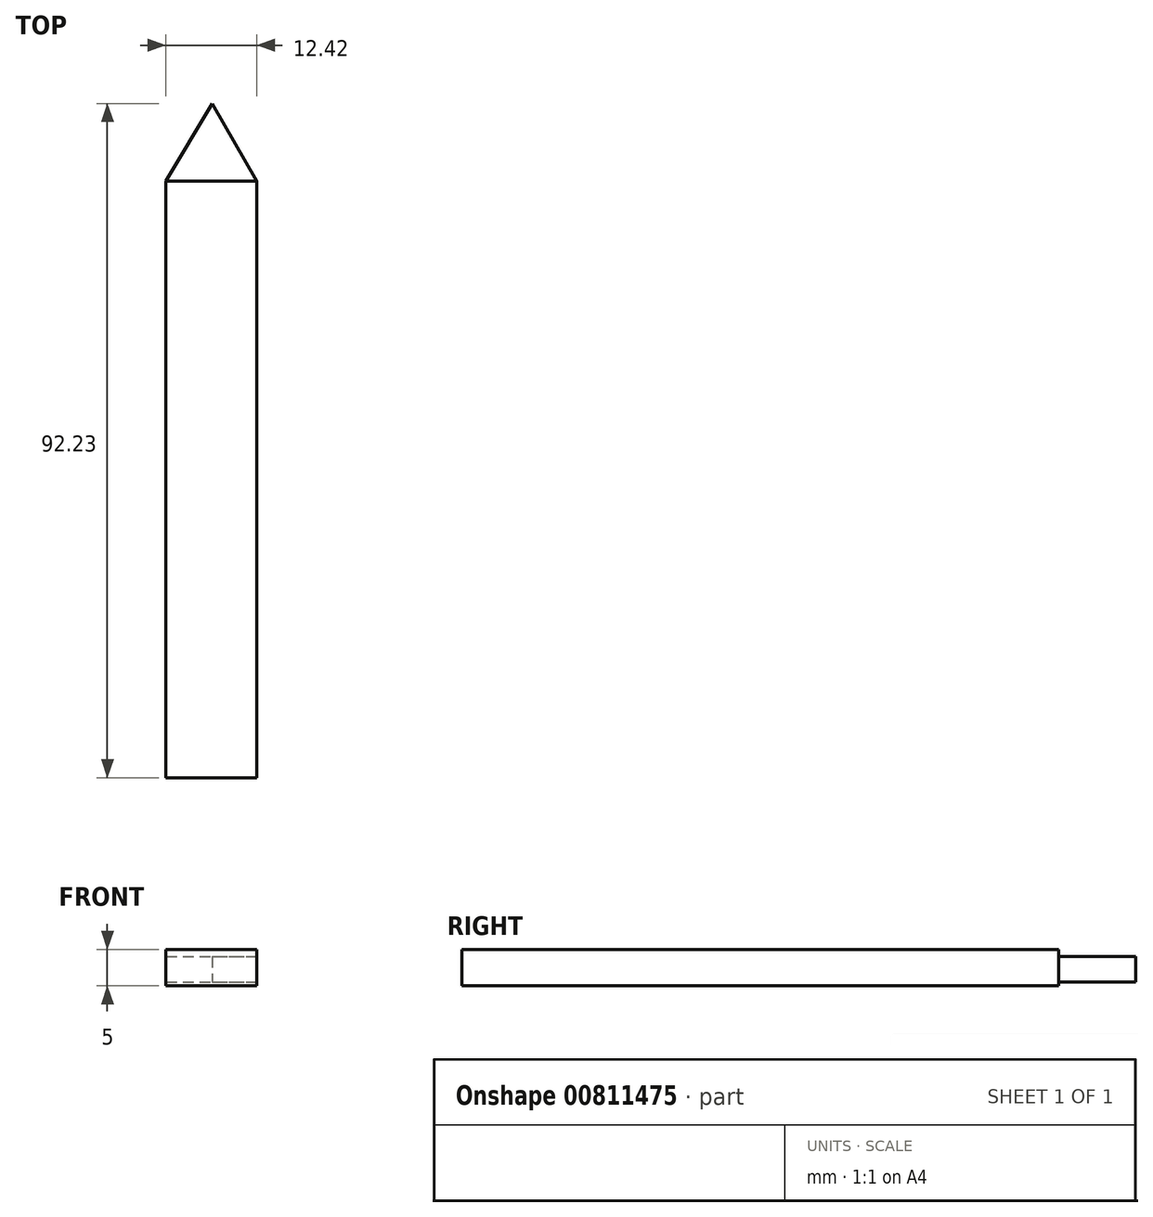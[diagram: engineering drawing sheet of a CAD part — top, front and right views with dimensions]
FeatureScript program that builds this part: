
annotation { "Feature Type Name" : "Feature", "Feature Type Description" : "" }
export const myFeature = defineFeature(function(context is Context, id is Id, definition is map)
    precondition{}
    {
        {
            var Q0;
            Q0=qCreatedBy(makeId("Top.planeOp"),FACE);
            var sketch = newSketch(context, id + "F0", { "sketchPlane" : qUnion([Q0])});
            skLineSegment(sketch, "E0.bottom", {"start": v(-52.46, -30.52) * mm, "end": v(-40.04, -30.52) * mm});
            skLineSegment(sketch, "E0.top", {"start": v(-52.46, 51.13) * mm, "end": v(-40.04, 51.13) * mm});
            skLineSegment(sketch, "E0.left", {"start": v(-52.46, -30.52) * mm, "end": v(-52.46, 51.13) * mm});
            skLineSegment(sketch, "E0.right", {"start": v(-40.04, -30.52) * mm, "end": v(-40.04, 51.13) * mm});
            skLineSegment(sketch, "E1", {"start": v(-52.46, 51.13) * mm, "end": v(-46.11, 61.7) * mm});
            skLineSegment(sketch, "E2", {"start": v(-46.11, 61.7) * mm, "end": v(-40.04, 51.13) * mm});
            skSolve(sketch);
        }
        {
            var Q0;
            Q0=makeQuery(id+"F0.imprint","IMPRINT",FACE,{"disambiguationData":[TD([[makeQuery(id+"F0.imprint","IMPRINT",EDGE,{"derivedFrom":sQuery(id+"F0.wireOp",EDGE,"E0.bottom")}),1.0]])]});
            extrude(context, id + "F1", {"entities" : qUnion([Q0]), "depth" : 2.5 * mm, "offsetDistance" : 25 * mm});
        }
        {
            var Q0;
            Q0=makeQuery(id+"F0.imprint","IMPRINT",FACE,{"disambiguationData":[TD([[makeQuery(id+"F0.imprint","IMPRINT",EDGE,{"derivedFrom":sQuery(id+"F0.wireOp",EDGE,"E0.top")}),1.0]])]});
            extrude(context, id + "F2", {"entities" : qUnion([Q0]), "operationType" : NewBodyOperationType.ADD, "depth" : 1.5 * mm, "offsetDistance" : 25 * mm});
        }
        {
            var Q0;
            Q0=makeQuery(id+"F1.opExtrude","CAP_FACE",FACE,{"disambiguationData":[OSD([sQuery(id+"F0.wireOp",EDGE,"E0.bottom"),sQuery(id+"F0.wireOp",EDGE,"E0.top"),sQuery(id+"F0.wireOp",EDGE,"E0.left"),sQuery(id+"F0.wireOp",EDGE,"E0.right")])],"isStart":false});
            extrude(context, id + "F3", {"entities" : qUnion([Q0]), "operationType" : NewBodyOperationType.ADD, "oppositeDirection" : true, "depth" : 5 * mm, "offsetDistance" : 25 * mm});
        }
        {
            var Q0;
            Q0=makeQuery(id+"F0.imprint","IMPRINT",FACE,{"disambiguationData":[TD([[makeQuery(id+"F0.imprint","IMPRINT",EDGE,{"derivedFrom":sQuery(id+"F0.wireOp",EDGE,"E0.top")}),1.0]])]});
            extrude(context, id + "F4", {"entities" : qUnion([Q0]), "operationType" : NewBodyOperationType.ADD, "oppositeDirection" : true, "depth" : 2 * mm, "offsetDistance" : 25 * mm});
        }
    });
